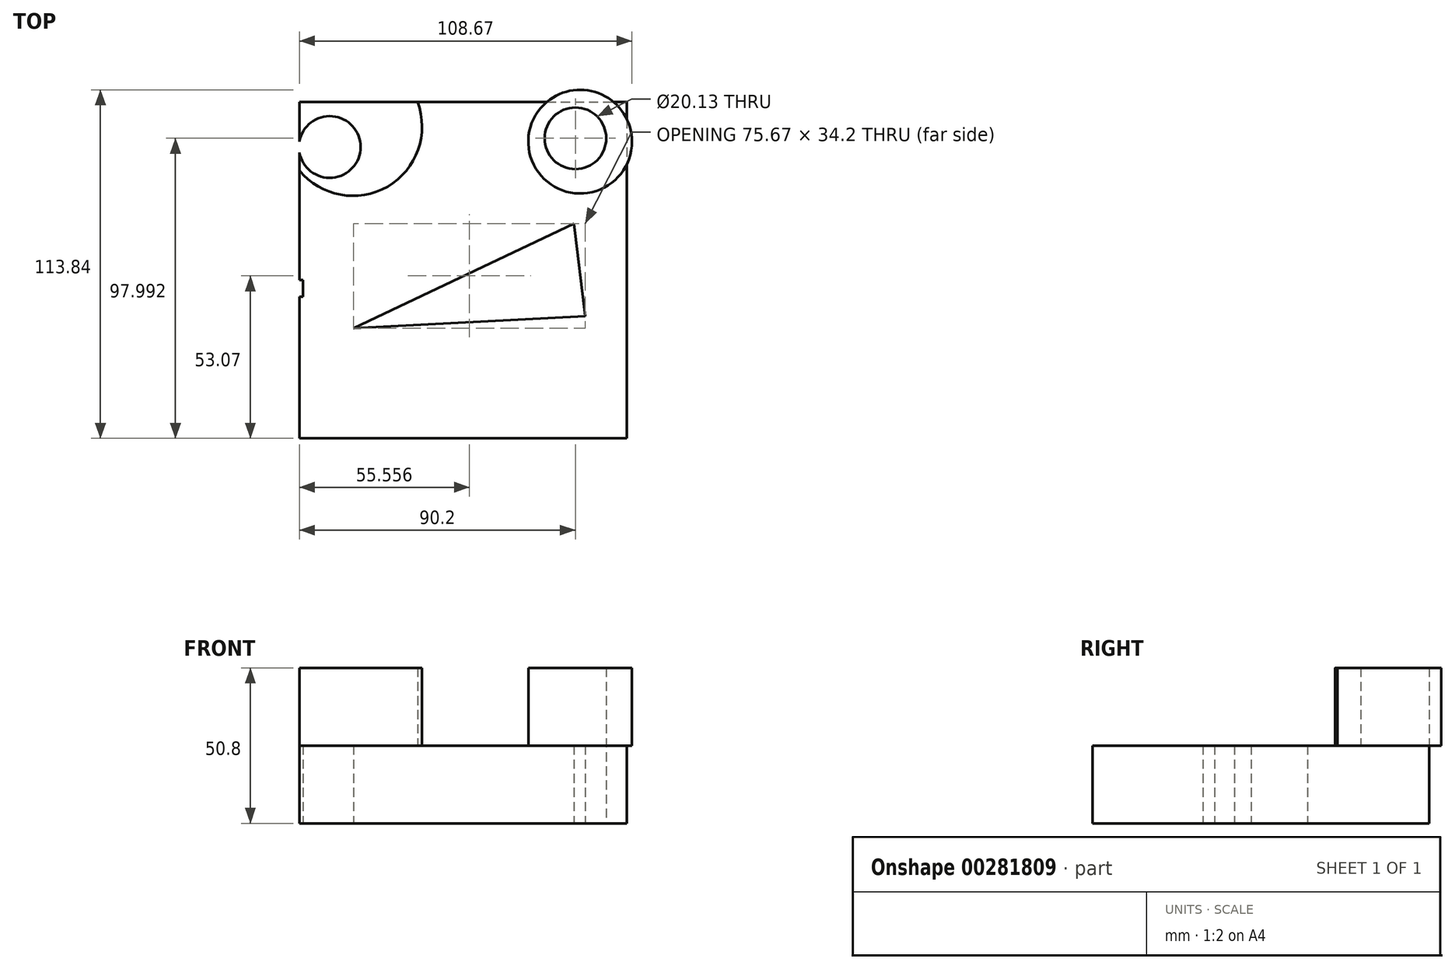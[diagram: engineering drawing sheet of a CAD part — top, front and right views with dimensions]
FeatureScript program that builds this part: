
annotation { "Feature Type Name" : "Feature", "Feature Type Description" : "" }
export const myFeature = defineFeature(function(context is Context, id is Id, definition is map)
    precondition{}
    {
        {
            var Q0;
            Q0=qCreatedBy(makeId("Top.planeOp"),FACE);
            var sketch = newSketch(context, id + "F0", { "sketchPlane" : qUnion([Q0])});
            skLineSegment(sketch, "E0.bottom", {"start": v(-62.9, 55.56) * mm, "end": v(44.13, 55.56) * mm});
            skLineSegment(sketch, "E0.top", {"start": v(-62.9, -54.31) * mm, "end": v(44.13, -54.31) * mm});
            skLineSegment(sketch, "E0.left", {"start": v(-62.9, 55.56) * mm, "end": v(-62.9, -54.31) * mm});
            skLineSegment(sketch, "E0.right", {"start": v(44.13, 55.56) * mm, "end": v(44.13, -54.31) * mm});
            skCircle(sketch, "E1", {"center": v(-52.99, 40.85) * mm, "radius": 10.08 * mm});
            skCircle(sketch, "E2", {"center": v(27.3, 43.68) * mm, "radius": 10.07 * mm});
            skLineSegment(sketch, "E3", {"start": v(-45.19, -18.34) * mm, "end": v(30.48, -14.44) * mm});
            skLineSegment(sketch, "E4", {"start": v(30.48, -14.44) * mm, "end": v(26.76, 15.86) * mm});
            skLineSegment(sketch, "E5", {"start": v(26.76, 15.86) * mm, "end": v(-45.19, -18.34) * mm});
            skLineSegment(sketch, "E6.bottom", {"start": v(-62.9, -54.31) * mm, "end": v(-55.11, -54.31) * mm});
            skLineSegment(sketch, "E6.top", {"start": v(-62.9, -75.93) * mm, "end": v(-55.11, -75.93) * mm});
            skLineSegment(sketch, "E6.left", {"start": v(-62.9, -54.31) * mm, "end": v(-62.9, -75.93) * mm});
            skLineSegment(sketch, "E6.right", {"start": v(-55.11, -54.31) * mm, "end": v(-55.11, -75.93) * mm});
            skLineSegment(sketch, "E7.bottom", {"start": v(44.13, -54.31) * mm, "end": v(34.91, -54.31) * mm});
            skLineSegment(sketch, "E7.top", {"start": v(44.13, -75.76) * mm, "end": v(34.91, -75.76) * mm});
            skLineSegment(sketch, "E7.left", {"start": v(44.13, -54.31) * mm, "end": v(44.13, -75.76) * mm});
            skLineSegment(sketch, "E7.right", {"start": v(34.91, -54.31) * mm, "end": v(34.91, -75.76) * mm});
            skLineSegment(sketch, "E8.bottom", {"start": v(44.13, 28.44) * mm, "end": v(71.95, 28.44) * mm});
            skLineSegment(sketch, "E8.top", {"start": v(44.13, 20.82) * mm, "end": v(71.95, 20.82) * mm});
            skLineSegment(sketch, "E8.left", {"start": v(44.13, 28.44) * mm, "end": v(44.13, 20.82) * mm});
            skLineSegment(sketch, "E8.right", {"start": v(71.95, 28.44) * mm, "end": v(71.95, 20.82) * mm});
            skLineSegment(sketch, "E9.bottom", {"start": v(-61.67, -8.06) * mm, "end": v(-77.44, -8.06) * mm});
            skLineSegment(sketch, "E9.top", {"start": v(-61.67, -2.57) * mm, "end": v(-77.44, -2.57) * mm});
            skLineSegment(sketch, "E9.left", {"start": v(-61.67, -8.06) * mm, "end": v(-61.67, -2.57) * mm});
            skLineSegment(sketch, "E9.right", {"start": v(-77.44, -8.06) * mm, "end": v(-77.44, -2.57) * mm});
            skLineSegment(sketch, "E10.bottom", {"start": v(-108.8, -10.9) * mm, "end": v(-107.03, -10.9) * mm});
            skLineSegment(sketch, "E10.top", {"start": v(-108.8, -13.73) * mm, "end": v(-107.03, -13.73) * mm});
            skLineSegment(sketch, "E10.left", {"start": v(-108.8, -10.9) * mm, "end": v(-108.8, -13.73) * mm});
            skLineSegment(sketch, "E10.right", {"start": v(-107.03, -10.9) * mm, "end": v(-107.03, -13.73) * mm});
            skSolve(sketch);
        }
        {
            var Q0;
            {var subQ10=sQuery(id+"F0.wireOp",EDGE,"E0.bottom");Q0=makeQuery(id+"F0.imprint","IMPRINT",FACE,{"disambiguationData":[TD([[makeQuery(id+"F0.imprint","IMPRINT",EDGE,{"derivedFrom":subQ10}),-1.0]])]});}
            extrude(context, id + "F1", {"entities" : qUnion([Q0]), "depth" : 25.4 * mm});
        }
        {
            var Q0;
            Q0=makeQuery(id+"F1.opExtrude","CAP_FACE",FACE,{"disambiguationData":[OSD([sQuery(id+"F0.wireOp",EDGE,"E0.bottom"),sQuery(id+"F0.wireOp",EDGE,"E0.top"),sQuery(id+"F0.wireOp",EDGE,"E0.left"),sQuery(id+"F0.wireOp",EDGE,"E0.right"),sQuery(id+"F0.wireOp",EDGE,"E1"),sQuery(id+"F0.wireOp",EDGE,"E2"),sQuery(id+"F0.wireOp",EDGE,"E3"),sQuery(id+"F0.wireOp",EDGE,"E4"),sQuery(id+"F0.wireOp",EDGE,"E5"),sQuery(id+"F0.wireOp",EDGE,"E6.bottom"),sQuery(id+"F0.wireOp",EDGE,"E7.bottom"),sQuery(id+"F0.wireOp",EDGE,"E8.left"),sQuery(id+"F0.wireOp",EDGE,"E9.bottom"),sQuery(id+"F0.wireOp",EDGE,"E9.top"),sQuery(id+"F0.wireOp",EDGE,"E9.left")])],"isStart":false});
            var sketch = newSketch(context, id + "F2", { "sketchPlane" : qUnion([Q0])});
            skCircle(sketch, "E11", {"center": v(-45.4, 47.47) * mm, "radius": 22.58 * mm});
            skCircle(sketch, "E12", {"center": v(28.82, 42.6) * mm, "radius": 16.94 * mm});
            skSolve(sketch);
        }
        {
            var Q0;
            {var subQ0=sQuery(id+"F2.wireOp",EDGE,"E12");var subQ1=makeQuery(id+"F1.opExtrude","CAP_EDGE",EDGE,{"disambiguationData":[OSD([sQuery(id+"F0.wireOp",EDGE,"E0.bottom")])],"isStart":false});var subQ2=makeQuery(id+"F2.imprint","INTERSECT",VERTEX,{"disambiguationData":[OD(0.0)],"derivedFrom":[subQ1,subQ0]});Q0=makeQuery(id+"F2.imprint","IMPRINT",FACE,{"disambiguationData":[TD([[makeQuery(id+"F2.imprint","IMPRINT",EDGE,{"disambiguationData":[TD([[subQ2,-1.0]])],"derivedFrom":subQ0}),1.0]])]});}
            var Q1;
            {var subQ0=sQuery(id+"F2.wireOp",EDGE,"E12");var subQ1=makeQuery(id+"F1.opExtrude","CAP_EDGE",EDGE,{"disambiguationData":[OSD([sQuery(id+"F0.wireOp",EDGE,"E0.right"),sQuery(id+"F0.wireOp",EDGE,"E8.left")])],"isStart":false});var subQ2=makeQuery(id+"F2.imprint","INTERSECT",VERTEX,{"disambiguationData":[OD(0.0)],"derivedFrom":[subQ1,subQ0]});Q1=makeQuery(id+"F2.imprint","IMPRINT",FACE,{"disambiguationData":[TD([[makeQuery(id+"F2.imprint","IMPRINT",EDGE,{"disambiguationData":[TD([[subQ2,1.0]])],"derivedFrom":subQ0}),1.0]])]});}
            var Q2;
            {var subQ2=sQuery(id+"F0.wireOp",EDGE,"E1");var subQ7=makeQuery(id+"F1.opExtrude","CAP_EDGE",EDGE,{"disambiguationData":[OSD([subQ2])],"isStart":false});Q2=makeQuery(id+"F2.imprint","IMPRINT",FACE,{"disambiguationData":[TD([[makeQuery(id+"F2.imprint","IMPRINT",EDGE,{"derivedFrom":subQ7}),-1.0]])]});}
            var Q3;
            Q3=makeQuery(id+"F2.imprint","IMPRINT",FACE,{"disambiguationData":[TD([[makeQuery(id+"F2.imprint","IMPRINT",EDGE,{"derivedFrom":makeQuery(id+"F1.opExtrude","CAP_EDGE",EDGE,{"disambiguationData":[OSD([sQuery(id+"F0.wireOp",EDGE,"E2")])],"isStart":false})}),-1.0]])]});
            extrude(context, id + "F3", {"entities" : qUnion([Q0, Q1, Q2, Q3]), "operationType" : NewBodyOperationType.ADD, "depth" : 25.4 * mm});
        }
    });
